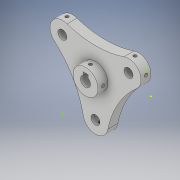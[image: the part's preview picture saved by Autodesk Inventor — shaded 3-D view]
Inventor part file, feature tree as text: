
AUTODESK INVENTOR PART (.ipt)
format: ipt  version: 2019 (Build 230136000, 136)  size: 259,584 bytes
history: native  units: mm
features: sketch x11, plane x10, hole x6, extrude x4, mirror x2, projected_geometry x2, other x1
ambient origin geometry x8: Origin, YZ Plane, XZ Plane, XY Plane, X Axis, Y Axis, Z Axis, Center Point
bodies: Body1 (feature_tree)
feature tree (36):
  other  "實體1"
  extrude  "擠出1"  Depth=109.5mm
  extrude  "擠出2"  Depth=43.5mm
  extrude  "擠出3"  Depth=76.5mm
  extrude  "擠出4"  Depth=25.0mm
  plane  "工作平面1"
  plane  "工作平面2"
  sketch  "草圖5"
  sketch  "草圖6"
  hole  "孔1"  [1 undecoded]
  hole  "孔2"  [1 undecoded]
  plane  "工作平面4"
  plane  "工作平面9"
  plane  "工作平面11"
  plane  "工作平面12"
  sketch  "草圖10"
  sketch  "草圖11"
  sketch  "草圖12"
  sketch  "草圖13"
  hole  "孔3"  [1 undecoded]
  hole  "孔4"  [1 undecoded]
  mirror  "鏡射1"
  hole  "孔5"  [1 undecoded]
  mirror  "鏡射2"
  plane  "工作平面14"
  plane  "工作平面15"
  hole  "孔7"  [1 undecoded]
  sketch  "草圖1"
  projected_geometry  "投影迴路1"
  sketch  "草圖3"
  sketch  "草圖4"
  projected_geometry  "投影迴路2"
  plane  "工作平面10"
  sketch  "草圖14"
  plane  "工作平面13"
  sketch  "草圖16"
note: 6 required parameter values undecoded (feature->parameter linkage not recoverable at this tier; creation-order binding heuristic only, values carry confidence <= 0.55)
